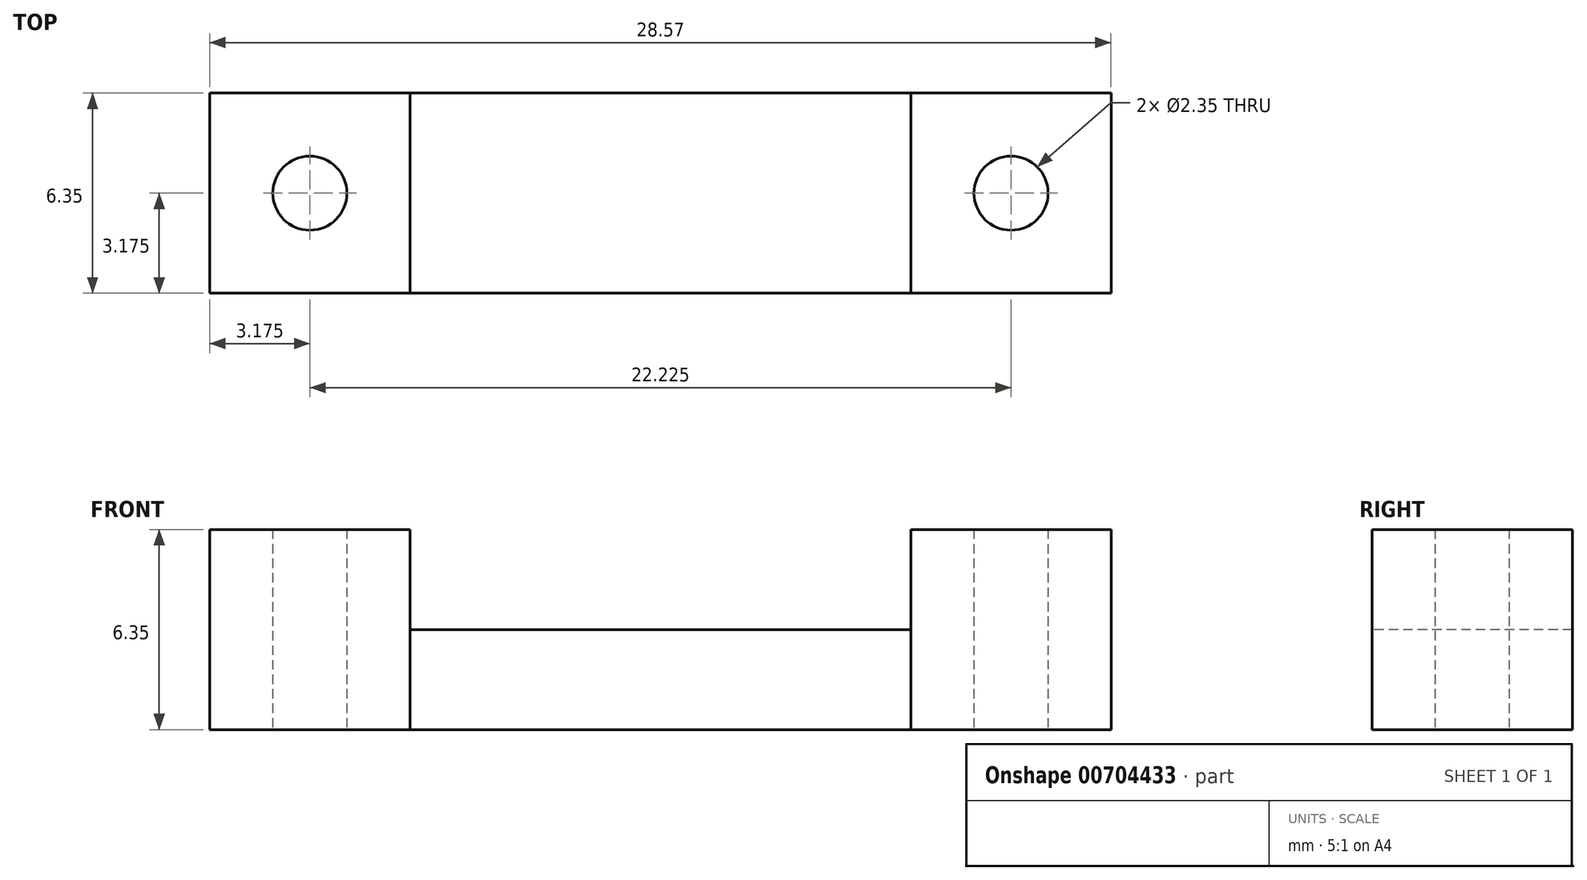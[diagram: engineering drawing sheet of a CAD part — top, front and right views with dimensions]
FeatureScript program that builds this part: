
annotation { "Feature Type Name" : "Feature", "Feature Type Description" : "" }
export const myFeature = defineFeature(function(context is Context, id is Id, definition is map)
    precondition{}
    {
        {
            var Q0;
            Q0=qCreatedBy(makeId("Top.planeOp"),FACE);
            var sketch = newSketch(context, id + "F0", { "sketchPlane" : qUnion([Q0])});
            skLineSegment(sketch, "E0.bottom", {"start": v(0, 0) * mm, "end": v(28.58, 0) * mm});
            skLineSegment(sketch, "E0.top", {"start": v(0, 6.35) * mm, "end": v(28.57, 6.35) * mm});
            skLineSegment(sketch, "E0.left", {"start": v(0, 0) * mm, "end": v(0, 6.35) * mm});
            skLineSegment(sketch, "E0.right", {"start": v(28.58, 0) * mm, "end": v(28.58, 6.35) * mm});
            skCircle(sketch, "E1", {"center": v(3.17, 3.17) * mm, "radius": 1.18 * mm});
            skLineSegment(sketch, "E2", {"start": v(6.35, 6.35) * mm, "end": v(6.35, 0) * mm});
            skLineSegment(sketch, "E3", {"start": v(14.29, 6.35) * mm, "end": v(14.29, 0) * mm});
            skLineSegment(sketch, "E4.MirrorCS", {"start": v(22.22, 6.35) * mm, "end": v(22.23, 0) * mm});
            skCircle(sketch, "E5.MirrorC", {"center": v(25.4, 3.18) * mm, "radius": 1.18 * mm});
            skSolve(sketch);
        }
        {
            var Q0;
            {var subQ0=sQuery(id+"F0.wireOp",EDGE,"E0.left");Q0=makeQuery(id+"F0.imprint","IMPRINT",FACE,{"disambiguationData":[TD([[makeQuery(id+"F0.imprint","IMPRINT",EDGE,{"derivedFrom":subQ0}),-1.0]])]});}
            var Q1;
            {var subQ0=sQuery(id+"F0.wireOp",EDGE,"E0.right");Q1=makeQuery(id+"F0.imprint","IMPRINT",FACE,{"disambiguationData":[TD([[makeQuery(id+"F0.imprint","IMPRINT",EDGE,{"derivedFrom":subQ0}),1.0]])]});}
            extrude(context, id + "F1", {"entities" : qUnion([Q0, Q1]), "depth" : 6.35 * mm, "offsetDistance" : 25.4 * mm});
        }
        {
            var Q0;
            {var subQ0=sQuery(id+"F0.wireOp",EDGE,"E2");Q0=makeQuery(id+"F0.imprint","IMPRINT",FACE,{"disambiguationData":[TD([[makeQuery(id+"F0.imprint","IMPRINT",EDGE,{"derivedFrom":subQ0}),1.0]])]});}
            var Q1;
            {var subQ0=sQuery(id+"F0.wireOp",EDGE,"E3");Q1=makeQuery(id+"F0.imprint","IMPRINT",FACE,{"disambiguationData":[TD([[makeQuery(id+"F0.imprint","IMPRINT",EDGE,{"derivedFrom":subQ0}),1.0]])]});}
            extrude(context, id + "F2", {"entities" : qUnion([Q0, Q1]), "depth" : 3.17 * mm, "offsetDistance" : 25.4 * mm});
        }
    });
